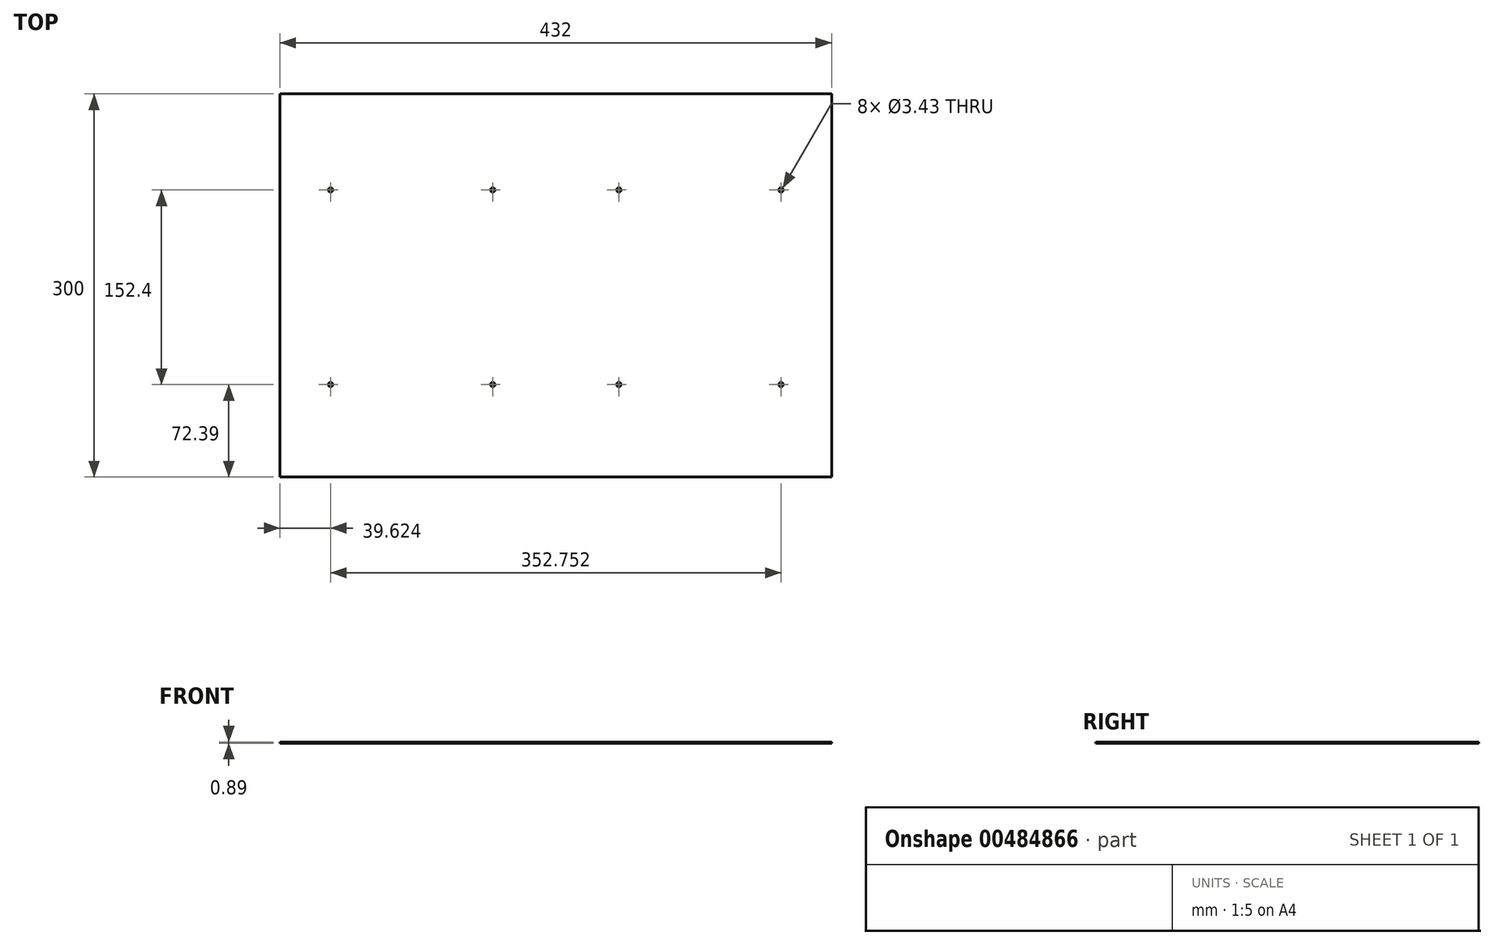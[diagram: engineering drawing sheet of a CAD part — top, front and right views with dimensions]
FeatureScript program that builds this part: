
annotation { "Feature Type Name" : "Feature", "Feature Type Description" : "" }
export const myFeature = defineFeature(function(context is Context, id is Id, definition is map)
    precondition{}
    {
        {
            var Q0;
            Q0=qCreatedBy(makeId("Top.planeOp"),FACE);
            var sketch = newSketch(context, id + "F0", { "sketchPlane" : qUnion([Q0])});
            skLineSegment(sketch, "E0.bottom", {"start": v(0, 0) * mm, "end": v(432, 0) * mm});
            skLineSegment(sketch, "E0.top", {"start": v(0, 300) * mm, "end": v(432, 300) * mm});
            skLineSegment(sketch, "E0.left", {"start": v(0, 0) * mm, "end": v(0, 300) * mm});
            skLineSegment(sketch, "E0.right", {"start": v(432, 0) * mm, "end": v(432, 300) * mm});
            skCircle(sketch, "E1", {"center": v(39.62, 72.4) * mm, "radius": 1.71 * mm});
            skLineSegment(sketch, "E2.bottom", {"start": v(39.62, 72.4) * mm, "end": v(166.62, 72.4) * mm, "construction": true});
            skLineSegment(sketch, "E2.top", {"start": v(39.62, 224.8) * mm, "end": v(166.62, 224.8) * mm, "construction": true});
            skLineSegment(sketch, "E2.left", {"start": v(39.62, 72.4) * mm, "end": v(39.62, 224.8) * mm, "construction": true});
            skLineSegment(sketch, "E2.right", {"start": v(166.62, 72.4) * mm, "end": v(166.62, 224.8) * mm, "construction": true});
            skCircle(sketch, "E3", {"center": v(39.62, 224.8) * mm, "radius": 1.71 * mm});
            skCircle(sketch, "E4", {"center": v(166.62, 224.8) * mm, "radius": 1.71 * mm});
            skCircle(sketch, "E5", {"center": v(166.62, 72.4) * mm, "radius": 1.71 * mm});
            skLineSegment(sketch, "E6", {"start": v(216, 300) * mm, "end": v(216, 0) * mm, "construction": true});
            skCircle(sketch, "E7.MirrorC", {"center": v(392.38, 224.8) * mm, "radius": 1.71 * mm});
            skCircle(sketch, "E8.MirrorC", {"center": v(265.38, 224.8) * mm, "radius": 1.71 * mm});
            skCircle(sketch, "E9.MirrorC", {"center": v(265.38, 72.4) * mm, "radius": 1.71 * mm});
            skCircle(sketch, "E10.MirrorC", {"center": v(392.38, 72.4) * mm, "radius": 1.71 * mm});
            skLineSegment(sketch, "E11.MirrorCS", {"start": v(265.38, 72.4) * mm, "end": v(265.38, 224.8) * mm, "construction": true});
            skLineSegment(sketch, "E12.MirrorCS", {"start": v(392.38, 224.8) * mm, "end": v(265.38, 224.8) * mm, "construction": true});
            skLineSegment(sketch, "E13.MirrorCS", {"start": v(392.38, 72.4) * mm, "end": v(392.38, 224.8) * mm, "construction": true});
            skLineSegment(sketch, "E14.MirrorCS", {"start": v(392.38, 72.4) * mm, "end": v(265.38, 72.4) * mm, "construction": true});
            skSolve(sketch);
        }
        {
            var Q0;
            Q0=makeQuery(id+"F0.imprint","IMPRINT",FACE,{"disambiguationData":[TD([[makeQuery(id+"F0.imprint","IMPRINT",EDGE,{"derivedFrom":sQuery(id+"F0.wireOp",EDGE,"E0.bottom")}),1.0]])]});
            extrude(context, id + "F1", {"entities" : qUnion([Q0]), "oppositeDirection" : true, "depth" : 0.89 * mm, "offsetDistance" : 25.4 * mm});
        }
    });
